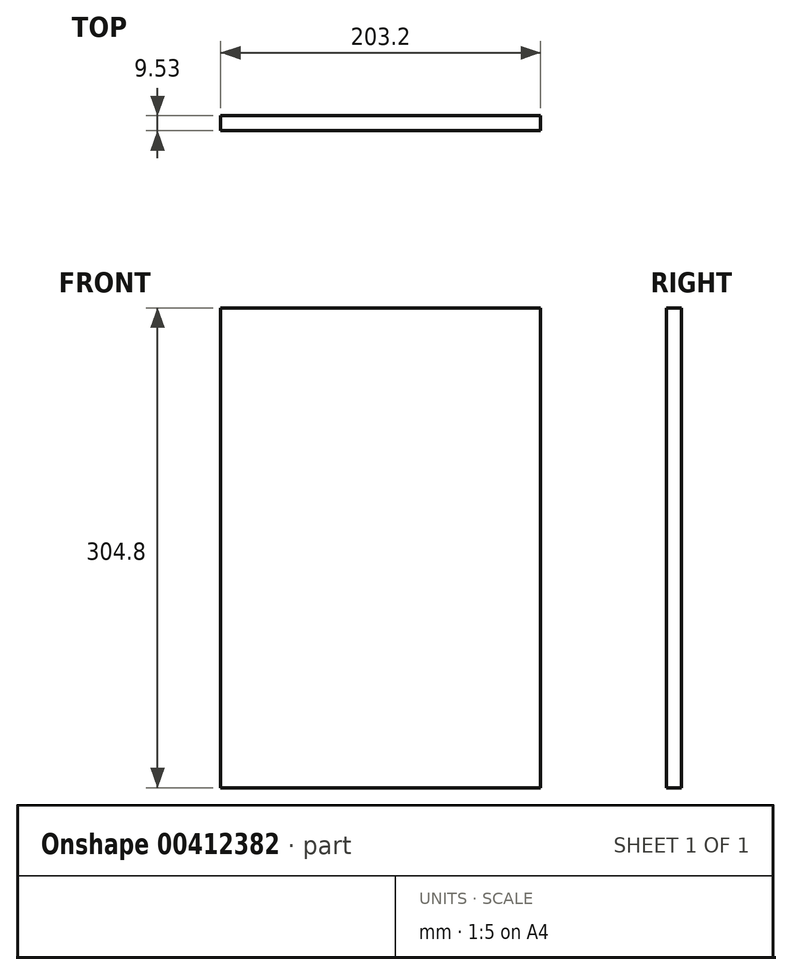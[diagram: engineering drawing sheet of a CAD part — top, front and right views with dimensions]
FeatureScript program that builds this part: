
annotation { "Feature Type Name" : "Feature", "Feature Type Description" : "" }
export const myFeature = defineFeature(function(context is Context, id is Id, definition is map)
    precondition{}
    {
        {
            var Q0;
            Q0=qCreatedBy(makeId("Front.planeOp"),FACE);
            var sketch = newSketch(context, id + "F0", { "sketchPlane" : qUnion([Q0])});
            skLineSegment(sketch, "E0.bottom", {"start": v(101.6, -152.4) * mm, "end": v(-101.6, -152.4) * mm});
            skLineSegment(sketch, "E0.top", {"start": v(101.6, 152.4) * mm, "end": v(-101.6, 152.4) * mm});
            skLineSegment(sketch, "E0.left", {"start": v(101.6, -152.4) * mm, "end": v(101.6, 152.4) * mm});
            skLineSegment(sketch, "E0.right", {"start": v(-101.6, -152.4) * mm, "end": v(-101.6, 152.4) * mm});
            skPoint(sketch, "E0.middle", {"position": v(0, 0) * mm});
            skSolve(sketch);
        }
        {
            var Q0;
            Q0 = qSketchRegion(id + "F0", true);
            extrude(context, id + "F1", {"entities" : qUnion([Q0]), "depth" : 9.52 * mm});
        }
    });
